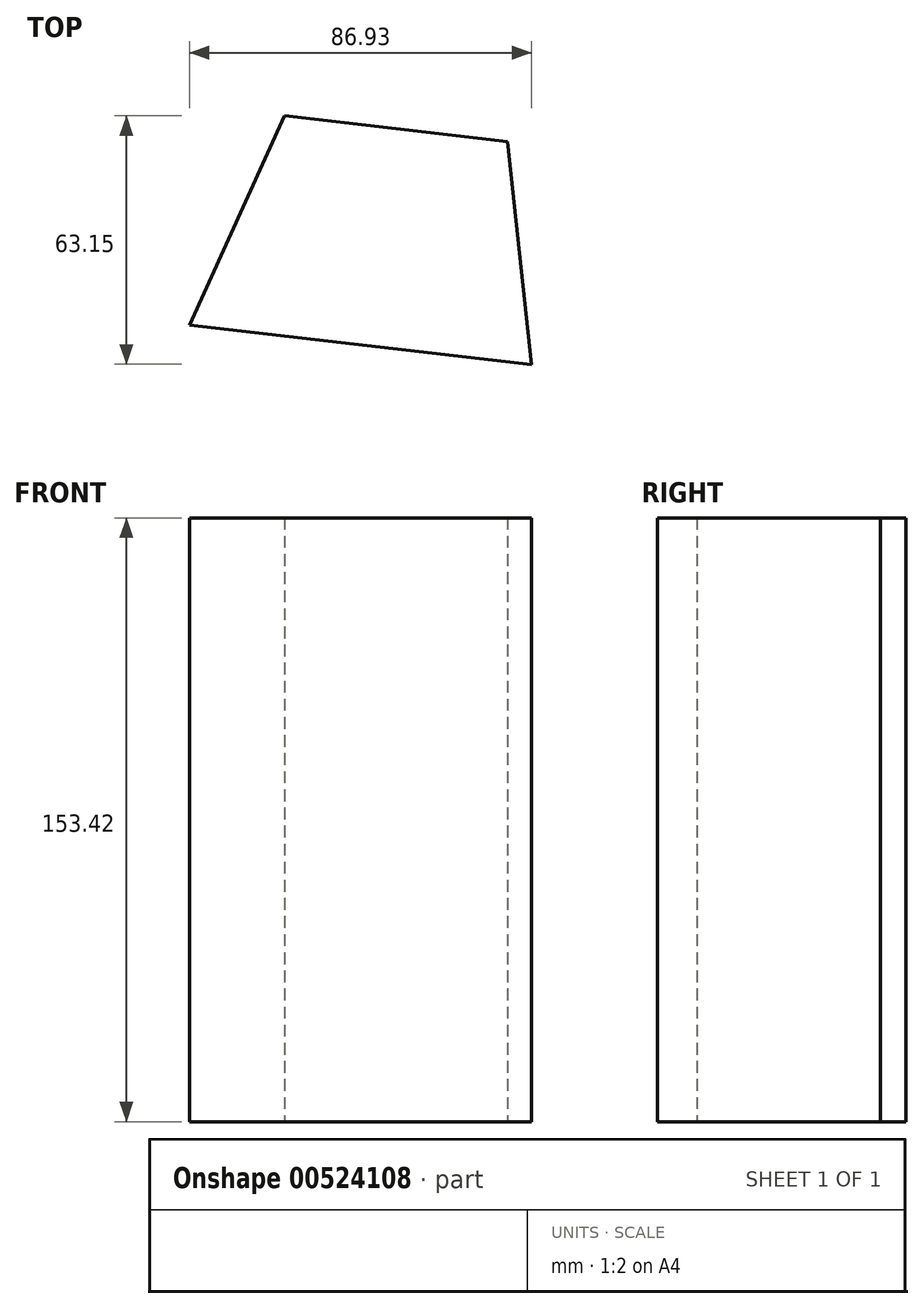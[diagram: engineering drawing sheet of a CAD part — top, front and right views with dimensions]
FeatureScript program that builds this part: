
annotation { "Feature Type Name" : "Feature", "Feature Type Description" : "" }
export const myFeature = defineFeature(function(context is Context, id is Id, definition is map)
    precondition{}
    {
        {
            var Q0;
            Q0=qCreatedBy(makeId("Top.planeOp"),FACE);
            var sketch = newSketch(context, id + "F0", { "sketchPlane" : qUnion([Q0])});
            skLineSegment(sketch, "E0", {"start": v(-117.75, -27.24) * mm, "end": v(-93.52, 25.93) * mm});
            skLineSegment(sketch, "E1", {"start": v(-93.52, 25.93) * mm, "end": v(-36.94, 19.41) * mm});
            skLineSegment(sketch, "E2", {"start": v(-36.94, 19.41) * mm, "end": v(-30.82, -37.22) * mm});
            skLineSegment(sketch, "E3", {"start": v(-30.82, -37.22) * mm, "end": v(-117.75, -27.24) * mm});
            skSolve(sketch);
        }
        {
            var Q0;
            Q0 = qSketchRegion(id + "F0", true);
            extrude(context, id + "F1", {"entities" : qUnion([Q0]), "depth" : 153.42 * mm, "offsetDistance" : 25.4 * mm});
        }
    });
